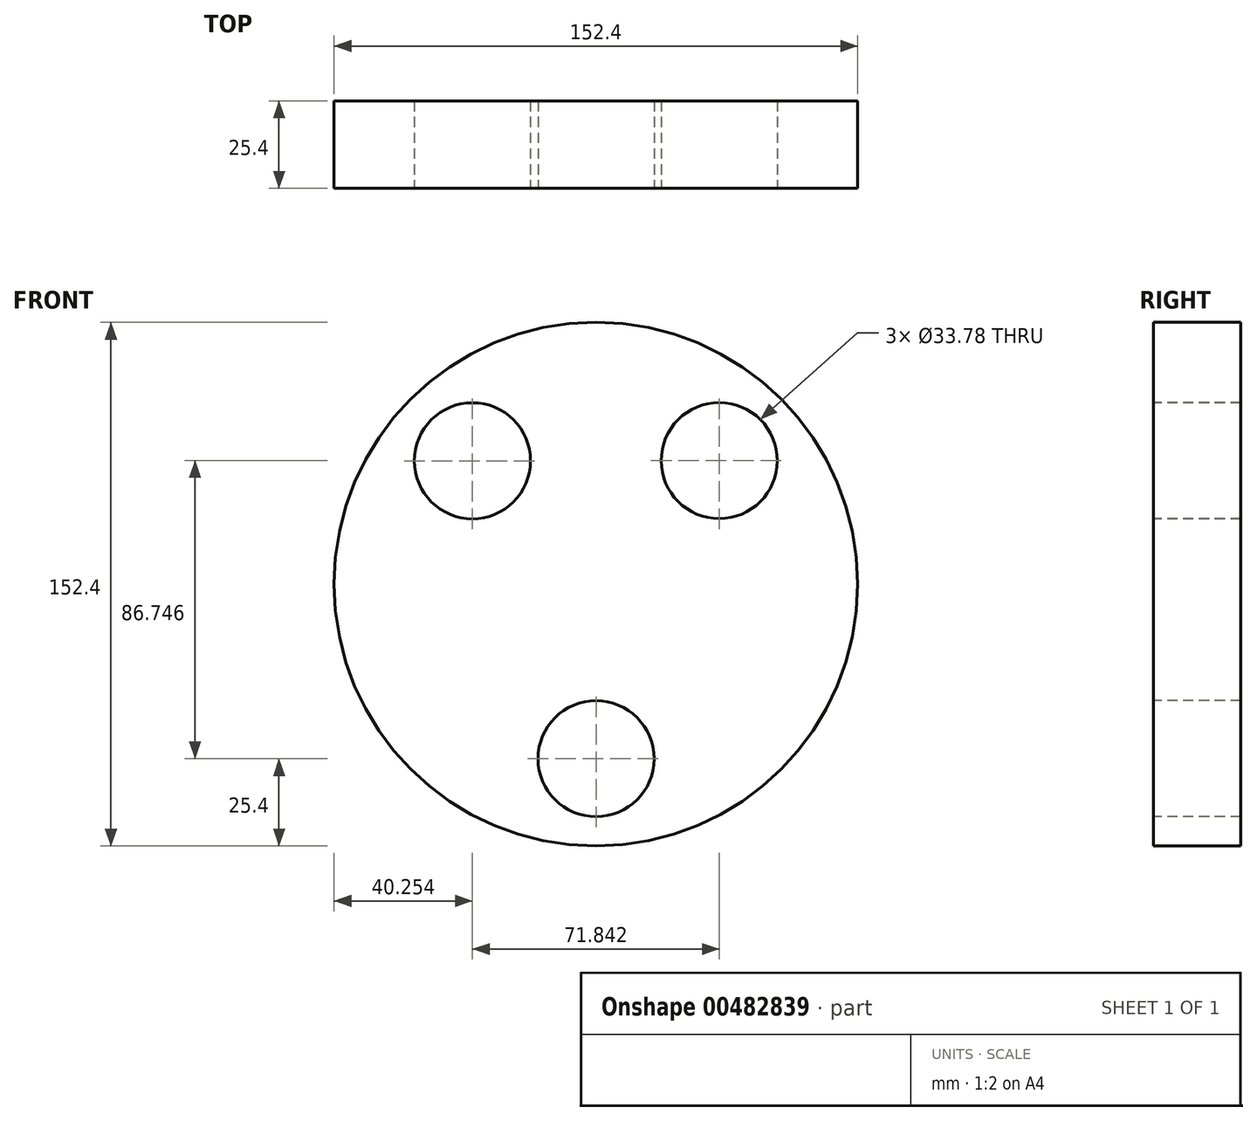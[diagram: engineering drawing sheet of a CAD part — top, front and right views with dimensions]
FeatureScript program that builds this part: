
annotation { "Feature Type Name" : "Feature", "Feature Type Description" : "" }
export const myFeature = defineFeature(function(context is Context, id is Id, definition is map)
    precondition{}
    {
        {
            var Q0;
            Q0=qCreatedBy(makeId("Front.planeOp"),FACE);
            var sketch = newSketch(context, id + "F0", { "sketchPlane" : qUnion([Q0])});
            skCircle(sketch, "E0", {"center": v(0, 0) * mm, "radius": 76.2 * mm});
            skSolve(sketch);
        }
        {
            var Q0;
            Q0=makeQuery(id+"F0.imprint","IMPRINT",FACE,{"disambiguationData":[TD([[makeQuery(id+"F0.imprint","IMPRINT",EDGE,{"derivedFrom":sQuery(id+"F0.wireOp",EDGE,"E0")}),1.0]])]});
            extrude(context, id + "F1", {"entities" : qUnion([Q0]), "depth" : 25.4 * mm});
        }
        {
            var Q0;
            Q0=makeQuery(id+"F1.opExtrude","CAP_FACE",FACE,{"disambiguationData":[OSD([sQuery(id+"F0.wireOp",EDGE,"E0")])],"isStart":false});
            var sketch = newSketch(context, id + "F2", { "sketchPlane" : qUnion([Q0])});
            skCircle(sketch, "E1", {"center": v(-35.95, 35.9) * mm, "radius": 16.9 * mm});
            skCircle(sketch, "E2.3.0", {"center": v(0.03, -50.8) * mm, "radius": 16.9 * mm});
            skCircle(sketch, "E2.6.0", {"center": v(35.9, 35.95) * mm, "radius": 16.9 * mm});
            skPoint(sketch, "E2.center", {"position": v(0, 0) * mm});
            skSolve(sketch);
        }
        {
            var Q0;
            Q0 = qSketchRegion(id + "F2", true);
            extrude(context, id + "F3", {"entities" : qUnion([Q0]), "operationType" : NewBodyOperationType.REMOVE, "oppositeDirection" : true, "depth" : 25.4 * mm});
        }
    });
